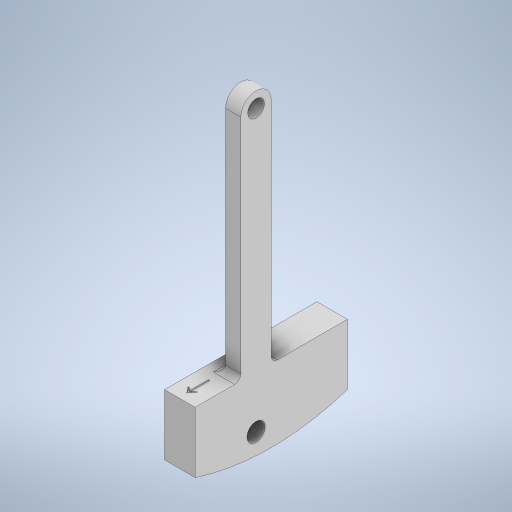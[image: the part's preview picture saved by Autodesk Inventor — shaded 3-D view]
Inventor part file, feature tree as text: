
AUTODESK INVENTOR PART (.ipt)
format: ipt  version: 2023 (Build 270158000, 158)  size: 295,936 bytes
history: native  units: mm
features: sketch x5, extrude x3, hole x2, fillet x2, other x1
ambient origin geometry x8: Origin, YZ Plane, XZ Plane, XY Plane, X Axis, Y Axis, Z Axis, Center Point
bodies: Body1 (feature_tree)
feature tree (13):
  other  "ソリッド1"
  extrude  "押し出し1"  Depth=20.0mm
  extrude  "押し出し2"  Depth=50.0mm
  hole  "穴1"  [1 undecoded]
  hole  "穴2"  [1 undecoded]
  fillet  "フィレット1"  Radius=80.0mm
  fillet  "フィレット2"  Radius=10.0mm
  extrude  "押し出し3"  Depth=5.0mm TaperAngle=0.0deg
  sketch  "スケッチ1"
  sketch  "スケッチ2"
  sketch  "スケッチ3"
  sketch  "スケッチ4"
  sketch  "スケッチ5"
note: 2 required parameter values undecoded (feature->parameter linkage not recoverable at this tier; creation-order binding heuristic only, values carry confidence <= 0.55)
